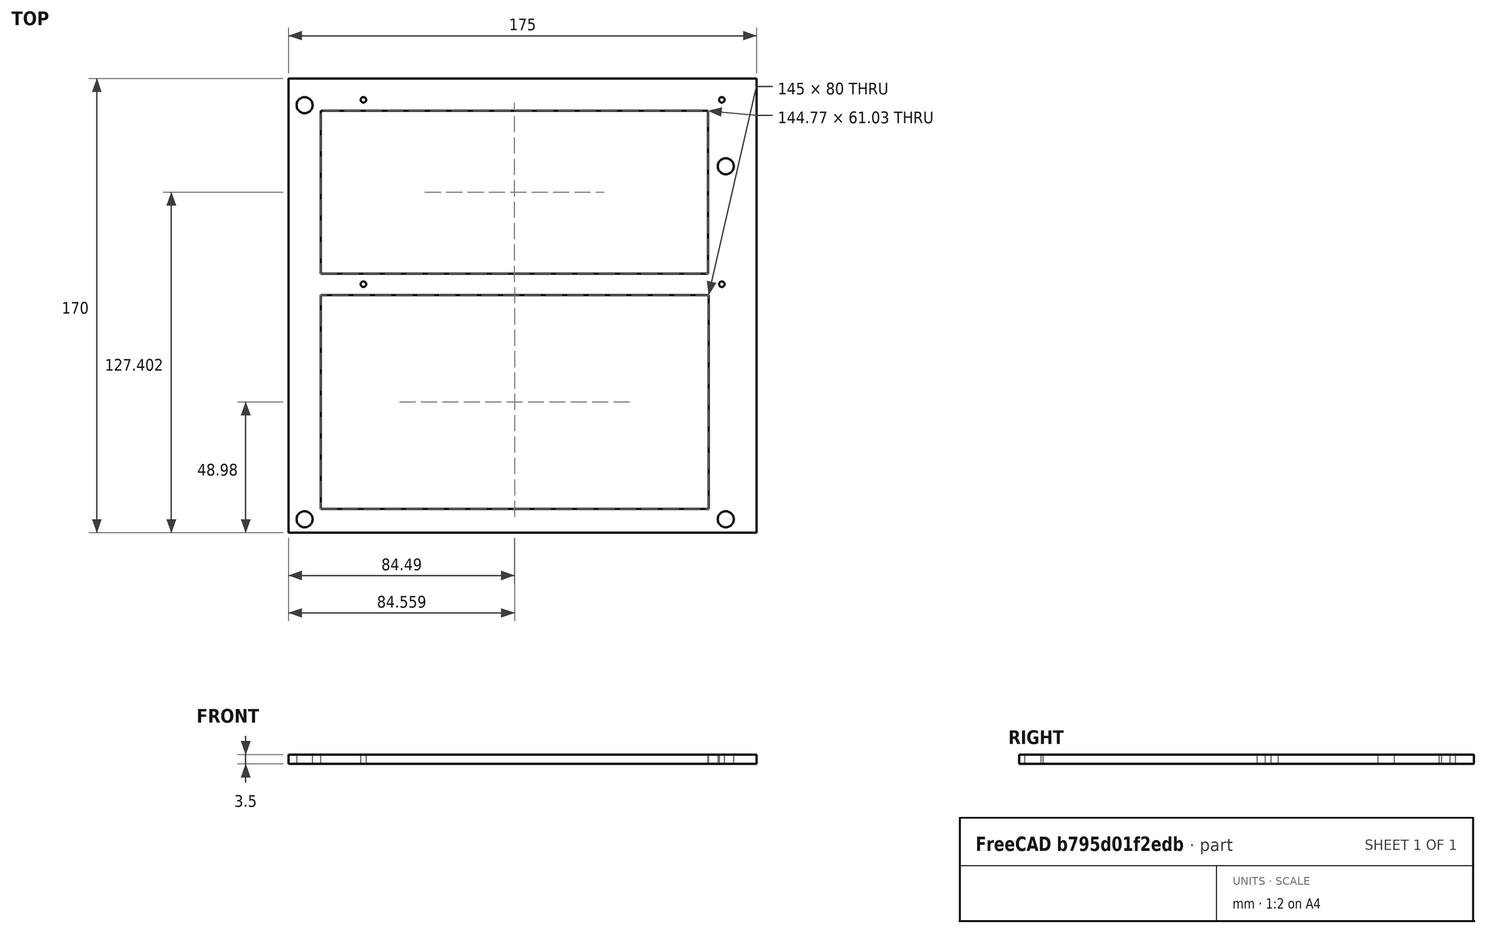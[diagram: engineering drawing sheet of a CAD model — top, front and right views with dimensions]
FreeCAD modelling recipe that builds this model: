
FCSTD DOCUMENT  (FreeCAD 0.20R29177 (Git))
Label: RPI_CM4_ITX_Adapter_Plate
License: Creative Commons Attribution
LicenseURL: http://creativecommons.org/licenses/by/4.0/
objects: Sketcher::SketchObject×1, PartDesign::Pad×1, PartDesign::Body×1
note: 4 computed .brp shape members not serialized (recipe doc carries the construction recipe); baked Part::Feature solids carry a one-line shape summary decoded from their .brp

FEATURE [Sketcher::SketchObject] Sketch
  FullyConstrained = false
  MapMode = 5
  Support = -> [XY_Plane]
  sketch-geometry (20):
    g0: LineSegment StartX=-6.00482 StartY=10 StartZ=0 EndX=-6.00482 EndY=-160 EndZ=0
    g1: LineSegment StartX=-6.00482 StartY=10 StartZ=0 EndX=168.995 EndY=10 EndZ=0
    g2: LineSegment StartX=168.995 StartY=10 StartZ=0 EndX=168.995 EndY=-160 EndZ=0
    g3: Circle CenterX=0 CenterY=0 CenterZ=0 NormalX=0 NormalY=0 NormalZ=1 AngleXU=0 Radius=3
    g4: Circle CenterX=0 CenterY=-154.94 CenterZ=0 NormalX=0 NormalY=0 NormalZ=1 AngleXU=0 Radius=3
    g5: Circle CenterX=157.48 CenterY=-22.86 CenterZ=0 NormalX=0 NormalY=0 NormalZ=1 AngleXU=0 Radius=3
    g6: Circle CenterX=157.48 CenterY=-154.94 CenterZ=0 NormalX=0 NormalY=0 NormalZ=1 AngleXU=0 Radius=3
    g7: LineSegment StartX=-6.00482 StartY=-160 StartZ=0 EndX=168.995 EndY=-160 EndZ=0
    g8: Circle CenterX=22 CenterY=2 CenterZ=0 NormalX=0 NormalY=0 NormalZ=1 AngleXU=0 Radius=1.025
    g9: Circle CenterX=156 CenterY=2 CenterZ=0 NormalX=0 NormalY=0 NormalZ=1 AngleXU=0 Radius=1.025
    g10: Circle CenterX=22 CenterY=-67 CenterZ=0 NormalX=0 NormalY=0 NormalZ=1 AngleXU=0 Radius=1.025
    g11: Circle CenterX=156 CenterY=-67 CenterZ=0 NormalX=0 NormalY=0 NormalZ=1 AngleXU=0 Radius=1.025
    g12: LineSegment StartX=6.05889 StartY=-151.02 StartZ=0 EndX=151.059 EndY=-151.02 EndZ=0
    g13: LineSegment StartX=151.059 StartY=-151.02 StartZ=0 EndX=151.059 EndY=-71.0203 EndZ=0
    g14: LineSegment StartX=151.059 StartY=-71.0203 StartZ=0 EndX=6.05889 EndY=-71.0203 EndZ=0
    g15: LineSegment StartX=6.05889 StartY=-71.0203 StartZ=0 EndX=6.05889 EndY=-151.02 EndZ=0
    g16: LineSegment StartX=6.10236 StartY=-63.1141 StartZ=0 EndX=150.877 EndY=-63.1141 EndZ=0
    g17: LineSegment StartX=150.877 StartY=-63.1141 StartZ=0 EndX=150.877 EndY=-2.08109 EndZ=0
    g18: LineSegment StartX=150.877 StartY=-2.08109 StartZ=0 EndX=6.10236 EndY=-2.08109 EndZ=0
    g19: LineSegment StartX=6.10236 StartY=-2.08109 StartZ=0 EndX=6.10236 EndY=-63.1141 EndZ=0
  constraints (52):
    c: Vertical(g0)
    c: Vertical(g2)
    c: Coincident(g0,g1)
    c: Coincident(g1,g2)
    c: Block(g0)
    c: Coincident(g3,g-1)
    c: PointOnObject(g4,g-2)
    c: Diameter(g4) = 6
    c: Diameter(g3) = 6
    c: Distance(g4,g3) = 154.94
    c: Diameter(g5) = 6
    c: DistanceX(g-2,g5) = 157.48
    c: Distance(g5,g-1) = 22.86
    c: Diameter(g6) = 6
    c: Distance(g6,g-1) = 154.94
    c: Distance(g6,g-2) = 157.48
    c: Coincident(g7,g0)
    c: Horizontal(g7)
    c: DistanceX(g7,g7) = 175
    c: DistanceY(g0,g0) = 170
    c: Diameter(g8) = 2.05
    c: Block(g1)
    c: Distance(g8,g-2) = 22
    c: Distance(g1) = 175
    c: Distance(g8,g1) = 8
    c: Diameter(g9) = 2.05
    c: Distance(g9,g1) = 8
    c: Distance(g9,g8) = 134
    c: Diameter(g10) = 2.05
    c: Distance(g10,g8) = 69
    c: Diameter(g11) = 2.05
    c: Distance(g9,g11) = 69
    c: Distance(g10,g11) = 134
    c: DistanceY(g2,g2) = 170
    c: Coincident(g12,g13)
    c: Coincident(g13,g14)
    c: Coincident(g14,g15)
    c: Coincident(g15,g12)
    c: Horizontal(g12)
    c: Horizontal(g14)
    c: Vertical(g13)
    c: Vertical(g15)
    c: DistanceY(g15,g15) = 80
    c: DistanceX(g12,g12) = 145
    c: Coincident(g16,g17)
    c: Coincident(g17,g18)
    c: Coincident(g18,g19)
    c: Coincident(g19,g16)
    c: Horizontal(g16)
    c: Horizontal(g18)
    c: Vertical(g17)
    c: Vertical(g19)
FEATURE [PartDesign::Pad] Pad
  Direction = (0,0,1)
  Length = 3.5
  Length2 = 10
  Profile = -> Sketch
  ReferenceAxis = -> Sketch [N_Axis]
  Type = 0
FEATURE [PartDesign::Body] Body
  Group = -> [Sketch,Pad]
  Origin = -> Origin
  Tip = -> Pad
